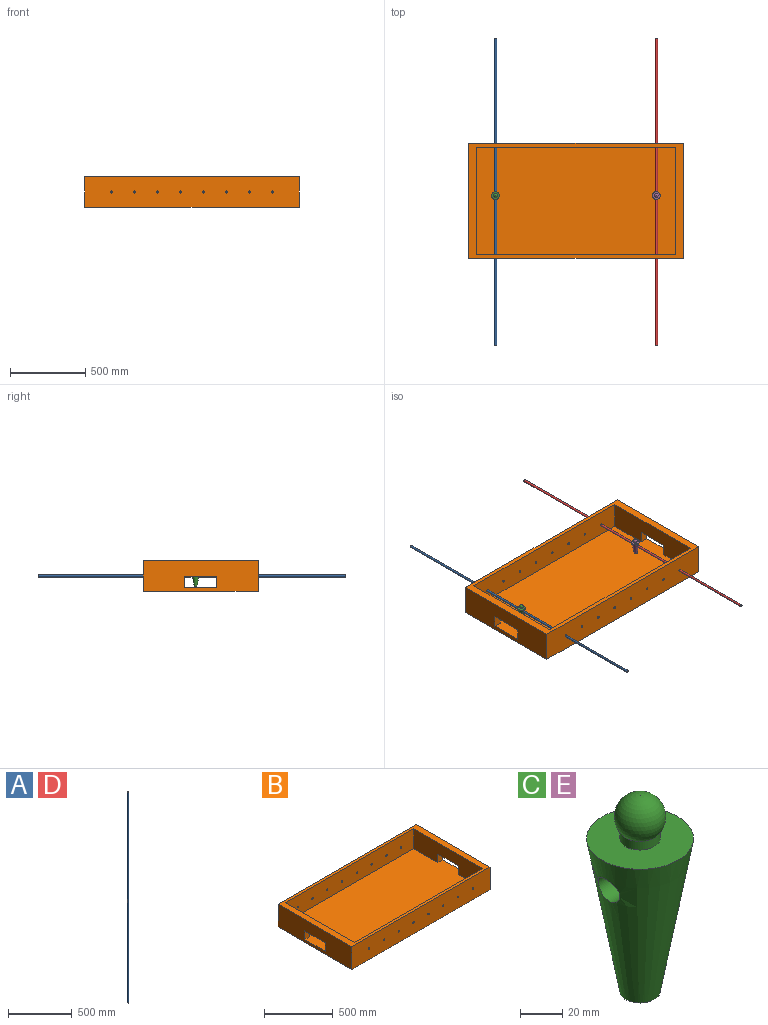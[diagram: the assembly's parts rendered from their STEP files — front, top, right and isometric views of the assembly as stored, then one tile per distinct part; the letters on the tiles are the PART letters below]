
ASSEMBLY  parts=5 mates=2
PART A: 3 faces, bbox 14.3x14.3x2032 mm
  f0: cylinder r=7.14mm len=2032mm, axis (0,0,-1), area 91207.3mm2, adj f1,f2
  f1: plane 14.29x14.29mm, normal (0,0,1), area 160.3mm2, adj f0
  f2: plane 14.29x14.29mm, normal (0,0,-1), area 160.3mm2, adj f0
PART B: 33 faces, bbox 1422.4x762x203.2 mm
  f0: plane 762x203.2mm, normal (-1,0,0), area 138628.8mm2, adj f2,f3,f4,f5,f10,f14,f15,f16
  f1: plane 762x203.2mm, normal (1,0,0), area 138628.8mm2, adj f2,f3,f4,f5,f10,f11,f12,f13
  f2: plane 1422.4x762mm, normal (0,0,1), area 144515.8mm2, adj f0,f1,f3,f4,f6,f7,f8,f9
  f3: plane 1422.4x203.2mm, normal (0,1,0), area 287749.1mm2, adj f0,f1,f2,f5,f18,f20,f24,f25
  f4: plane 1422.4x203.2mm, normal (0,-1,0), area 287749.1mm2, adj f0,f1,f2,f5,f17,f19,f21,f22
  f5: plane 1422.4x762mm, normal (0,0,-1), area 1083868.8mm2, adj f0,f1,f3,f4
  f6: plane 1320.8x177.8mm, normal (0,-1,0), area 233555.6mm2, adj f2,f7,f9,f10,f18,f20,f24,f25
  f7: plane 711.2x177.8mm, normal (1,0,0), area 110241.7mm2, adj f2,f6,f8,f10,f14,f15,f16
  f8: plane 1320.8x177.8mm, normal (0,1,0), area 233555.6mm2, adj f2,f7,f9,f10,f17,f19,f21,f22
  f9: plane 711.2x177.8mm, normal (-1,0,0), area 110241.7mm2, adj f2,f6,f8,f10,f11,f12,f13
  f10: plane 1422.4x711.2mm, normal (0,0,1), area 960965.8mm2, adj f0,f1,f6,f7,f8,f9,f11,f12
  f11: plane 76.2x50.8mm, normal (0,1,0), area 3871mm2, adj f1,f9,f10,f13
  f12: plane 76.2x50.8mm, normal (0,-1,0), area 3871mm2, adj f1,f9,f10,f13
  f13: plane 212.73x50.8mm, normal (0,0,-1), area 10806.4mm2, adj f1,f9,f11,f12
  f14: plane 212.73x50.8mm, normal (0,0,-1), area 10806.4mm2, adj f0,f7,f15,f16
  f15: plane 76.2x50.8mm, normal (0,1,0), area 3871mm2, adj f0,f7,f10,f14
  f16: plane 76.2x50.8mm, normal (0,-1,0), area 3871mm2, adj f0,f7,f10,f14
  f17: cylinder r=7.14mm len=25.4mm, axis (0,1,0), area 1140.1mm2, adj f4,f8
  f18: cylinder r=7.14mm len=25.4mm, axis (0,1,0), area 1140.1mm2, adj f3,f6
  f19: cylinder r=7.14mm len=25.4mm, axis (0,1,0), area 1140.1mm2, adj f4,f8
  f20: cylinder r=7.14mm len=25.4mm, axis (0,1,0), area 1140.1mm2, adj f3,f6
  f21: cylinder r=7.14mm len=25.4mm, axis (0,1,0), area 1140.1mm2, adj f4,f8
  f22: cylinder r=7.14mm len=25.4mm, axis (0,1,0), area 1140.1mm2, adj f4,f8
  f23: cylinder r=7.14mm len=25.4mm, axis (0,1,0), area 1140.1mm2, adj f4,f8
  f24: cylinder r=7.14mm len=25.4mm, axis (0,1,0), area 1140.1mm2, adj f3,f6
  f25: cylinder r=7.14mm len=25.4mm, axis (0,1,0), area 1140.1mm2, adj f3,f6
  f26: cylinder r=7.14mm len=25.4mm, axis (0,1,0), area 1140.1mm2, adj f3,f6
  f27: cylinder r=7.14mm len=25.4mm, axis (0,1,0), area 1140.1mm2, adj f4,f8
  f28: cylinder r=7.14mm len=25.4mm, axis (0,1,0), area 1140.1mm2, adj f4,f8
  f29: cylinder r=7.14mm len=25.4mm, axis (0,1,0), area 1140.1mm2, adj f4,f8
  f30: cylinder r=7.14mm len=25.4mm, axis (0,1,0), area 1140.1mm2, adj f3,f6
  f31: cylinder r=7.14mm len=25.4mm, axis (0,1,0), area 1140.1mm2, adj f3,f6
  f32: cylinder r=7.14mm len=25.4mm, axis (0,1,0), area 1140.1mm2, adj f3,f6
PART C: 6 faces, bbox 50.8x50.8x113.8 mm
  f0: sphere r=12.2mm, area 1518.9mm2, adj f4
  f1: plane 19.05x19.05mm, normal (0,0,-1), area 285mm2, adj f2
  f2: cone r=9.53mm half-angle=10.1deg, axis (0,0,1), area 9578.2mm2, adj f1,f3,f5
  f3: plane 50.8x50.8mm, normal (0,0,1), area 1741.8mm2, adj f2,f4
  f4: cylinder r=9.53mm len=19.05mm, axis (0,0,1), area 304mm2, adj f0,f3
  f5: cylinder r=7.14mm len=46.55mm, axis (1,0,0), area 1921.5mm2, adj f2
PART D: same geometry as A
PART E: same geometry as C
PLACE A rot(axis=(0.6,-0.57,0.57),118.5deg) t=(-1244.6,692.8,101.6)mm
PLACE B rot(axis=(0,1,0),0deg) t=(-711.2,-381,0)mm
PLACE C rot(axis=(-0.02,-0.02,1),90deg) t=(-1244.6,-346.76,101.6)mm
PLACE D rot(axis=(0.6,-0.57,0.57),118.5deg) t=(-177.8,692.8,101.6)mm
PLACE E rot(axis=(-0.02,-0.02,1),90deg) t=(-177.8,-346.76,101.6)mm
MATE revolute C.f5 <-> A.f0  axis (0,1,0) through (-1244.6,-323.2,101.6)mm
MATE cylindrical B.f21 <-> A.f0  axis (0,-1,0) through (-1244.6,-25.4,101.6)mm
